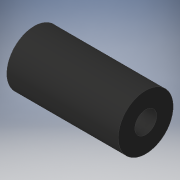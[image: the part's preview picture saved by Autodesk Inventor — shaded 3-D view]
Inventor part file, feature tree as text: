
AUTODESK INVENTOR PART (.ipt)
format: ipt  version: 2017 SP1 (Build 210196100, 196)  size: 95,232 bytes
history: native  units: in
note: dims shown in document units (in); Inventor stores cm internally (conversion verified against a paired STEP export)
features: extrude x1, sketch x1
ambient origin geometry x8: Origin, YZ Plane, XZ Plane, XY Plane, X Axis, Y Axis, Z Axis, Center Point
bodies: Solid1 (feature_tree)
feature tree (2):
  extrude  "Extrusion1"  Depth=14.0in
  sketch  "Sketch1"  dims[d0=6.9in d1=2.75in d2=14.0in d3=0.0in]
